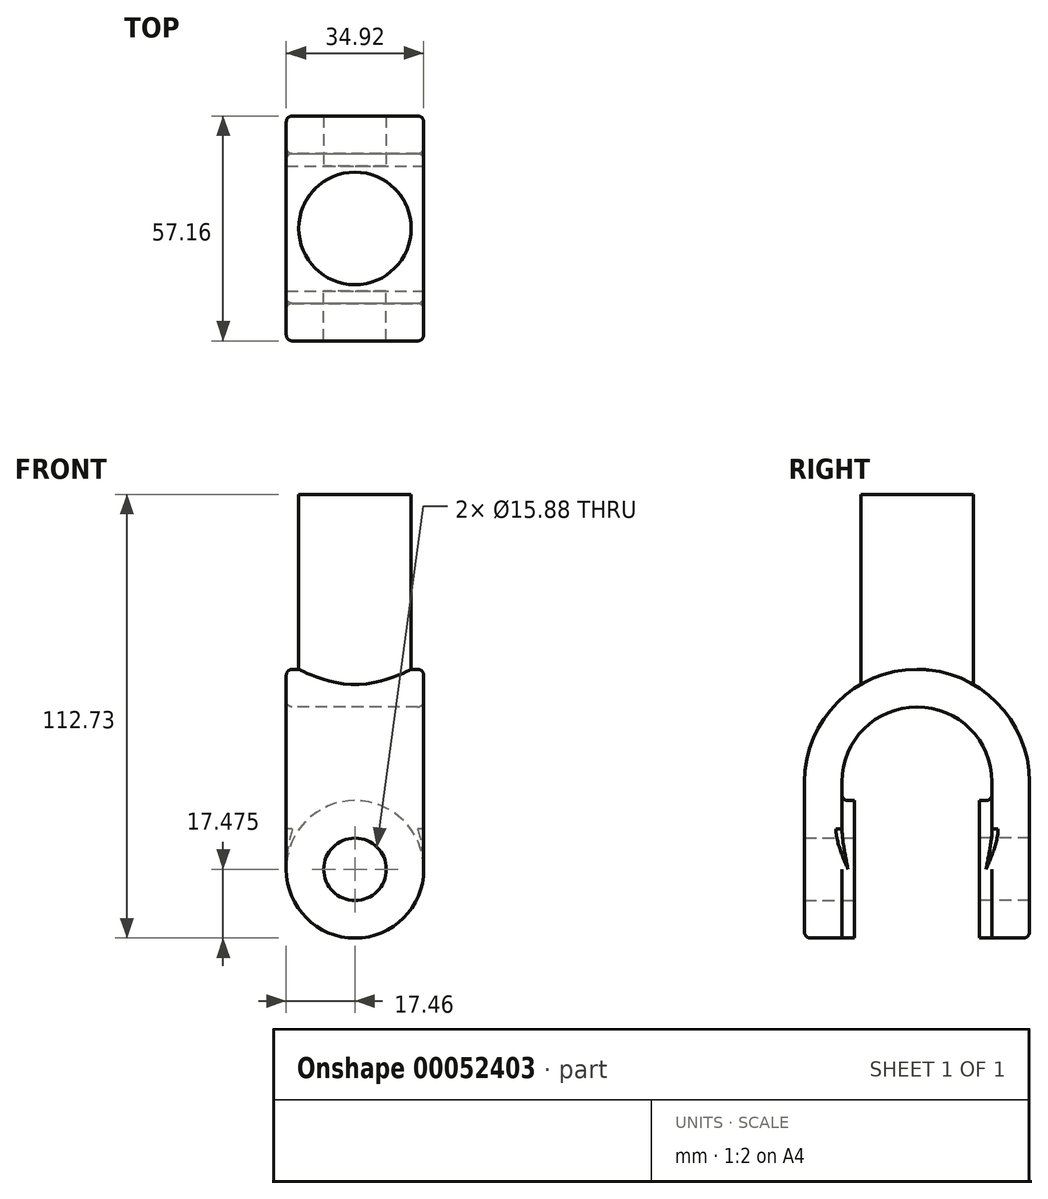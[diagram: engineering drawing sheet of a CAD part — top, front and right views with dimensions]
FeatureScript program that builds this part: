
annotation { "Feature Type Name" : "Feature", "Feature Type Description" : "" }
export const myFeature = defineFeature(function(context is Context, id is Id, definition is map)
    precondition{}
    {
        {
            var Q0;
            Q0=qCreatedBy(makeId("Right.planeOp"),FACE);
            var sketch = newSketch(context, id + "F0", { "sketchPlane" : qUnion([Q0])});
            skArc(sketch, "E0", {"start": v(19.05, 0) * mm, "mid": v(0, 19.05) * mm, "end": v(-19.05, 0) * mm});
            skArc(sketch, "E1.0", {"start": v(28.58, 0) * mm, "mid": v(0, 28.58) * mm, "end": v(-28.58, 0) * mm});
            skLineSegment(sketch, "E2", {"start": v(-28.58, 0) * mm, "end": v(-28.57, -39.7) * mm});
            skLineSegment(sketch, "E3", {"start": v(-28.57, -39.7) * mm, "end": v(-19.05, -39.7) * mm});
            skLineSegment(sketch, "E4", {"start": v(28.57, 0) * mm, "end": v(28.57, -39.7) * mm});
            skLineSegment(sketch, "E5", {"start": v(-19.05, 0) * mm, "end": v(-19.05, -39.7) * mm});
            skLineSegment(sketch, "E6", {"start": v(19.05, 0) * mm, "end": v(19.05, -39.7) * mm});
            skLineSegment(sketch, "E7.trimOffspring", {"start": v(19.05, -39.7) * mm, "end": v(28.57, -39.7) * mm});
            skSolve(sketch);
        }
        {
            var Q0;
            Q0=makeQuery(id+"F0.imprint","IMPRINT",FACE,{"disambiguationData":[TD([[makeQuery(id+"F0.imprint","IMPRINT",EDGE,{"derivedFrom":sQuery(id+"F0.wireOp",EDGE,"E0")}),-1.0]])]});
            extrude(context, id + "F1", {"entities" : qUnion([Q0]), "endBound" : BoundingType.SYMMETRIC, "depth" : 34.92 * mm});
        }
        {
            var Q0;
            Q0=qCreatedBy(makeId("Top.planeOp"),FACE);
            cPlane(context, id + "F2", {"entities" : qUnion([Q0]), "cplaneType" : CPlaneType.OFFSET, "offset" : 73.02 * mm, "width" : 152.4 * mm, "height" : 152.4 * mm});
        }
        {
            var Q0;
            Q0=qCreatedBy(id+"F2.planeOp",FACE);
            var sketch = newSketch(context, id + "F3", { "sketchPlane" : qUnion([Q0])});
            skCircle(sketch, "E8", {"center": v(0, 0) * mm, "radius": 14.29 * mm});
            skSolve(sketch);
        }
        {
            var Q0;
            Q0=makeQuery(id+"F3.imprint","IMPRINT",FACE,{"disambiguationData":[TD([[makeQuery(id+"F3.imprint","IMPRINT",EDGE,{"derivedFrom":sQuery(id+"F3.wireOp",EDGE,"E8")}),1.0]])]});
            extrude(context, id + "F4", {"entities" : qUnion([Q0]), "endBound" : BoundingType.UP_TO_NEXT, "oppositeDirection" : true, "depth" : 25.4 * mm});
        }
        {
            var Q0;
            Q0=makeQuery(id+"F1.opExtrude","CAP_EDGE",EDGE,{"disambiguationData":[OSD([sQuery(id+"F0.wireOp",EDGE,"E7.trimOffspring")])],"isStart":true});
            var Q1;
            Q1=makeQuery(id+"F1.opExtrude","CAP_EDGE",EDGE,{"disambiguationData":[OSD([sQuery(id+"F0.wireOp",EDGE,"E7.trimOffspring")])],"isStart":false});
            var Q2;
            Q2=makeQuery(id+"F1.opExtrude","CAP_EDGE",EDGE,{"disambiguationData":[OSD([sQuery(id+"F0.wireOp",EDGE,"E3")])],"isStart":true});
            var Q3;
            Q3=makeQuery(id+"F1.opExtrude","CAP_EDGE",EDGE,{"disambiguationData":[OSD([sQuery(id+"F0.wireOp",EDGE,"E3")])],"isStart":false});
            fillet(context, id + "F5", {"entities" : qUnion([Q0, Q1, Q2, Q3]), "radius" : 17.46 * mm, "tangentPropagation" : true, "allowEdgeOverflow" : false});
        }
        {
            var Q0;
            Q0=makeQuery(id+"F1.opExtrude","SWEPT_FACE",FACE,{"disambiguationData":[OSD([sQuery(id+"F0.wireOp",EDGE,"E6")])]});
            var sketch = newSketch(context, id + "F6", { "sketchPlane" : qUnion([Q0])});
            skCircle(sketch, "E9", {"center": v(0, -22.22) * mm, "radius": 17.46 * mm});
            skSolve(sketch);
        }
        {
            var Q0;
            Q0 = qSketchRegion(id + "F6", true);
            extrude(context, id + "F7", {"entities" : qUnion([Q0]), "operationType" : NewBodyOperationType.ADD, "depth" : 3.17 * mm});
        }
        {
            var Q0;
            Q0=makeQuery(id+"F1.opExtrude","SWEPT_BODY",BODY,{"disambiguationData":[OSD([sQuery(id+"F0.wireOp",EDGE,"E0"),sQuery(id+"F0.wireOp",EDGE,"E1.0"),sQuery(id+"F0.wireOp",EDGE,"E2"),sQuery(id+"F0.wireOp",EDGE,"E3"),sQuery(id+"F0.wireOp",EDGE,"E4"),sQuery(id+"F0.wireOp",EDGE,"E5"),sQuery(id+"F0.wireOp",EDGE,"E6"),sQuery(id+"F0.wireOp",EDGE,"E7.trimOffspring")])]});
            var Q1;
            Q1=qCreatedBy(makeId("Front.planeOp"),FACE);
            mirror(context, id + "F8", {"operationType" : NewBodyOperationType.ADD, "entities" : qUnion([Q0]), "mirrorPlane" : qUnion([Q1])});
        }
        {
            var Q0;
            Q0=makeQuery(id+"F7.opExtrude","CAP_FACE",FACE,{"disambiguationData":[OSD([sQuery(id+"F6.wireOp",EDGE,"E9")])],"isStart":false});
            var sketch = newSketch(context, id + "F9", { "sketchPlane" : qUnion([Q0])});
            skCircle(sketch, "E10", {"center": v(0, -22.22) * mm, "radius": 7.94 * mm});
            skSolve(sketch);
        }
        {
            var Q0;
            Q0 = qSketchRegion(id + "F9", true);
            extrude(context, id + "F10", {"entities" : qUnion([Q0]), "operationType" : NewBodyOperationType.REMOVE, "endBound" : BoundingType.THROUGH_ALL, "oppositeDirection" : true, "depth" : 25.4 * mm});
        }
        {
            var Q0;
            Q0=makeQuery(id+"F8.opPattern","COPY",FACE,{"derivedFrom":makeQuery(id+"F7.opExtrude","CAP_FACE",FACE,{"disambiguationData":[OSD([sQuery(id+"F6.wireOp",EDGE,"E9")])],"isStart":false}),"instanceName":"1"});
            var sketch = newSketch(context, id + "F11", { "sketchPlane" : qUnion([Q0])});
            skCircle(sketch, "E11", {"center": v(0, -22.22) * mm, "radius": 7.94 * mm});
            skSolve(sketch);
        }
        {
            var Q0;
            Q0 = qSketchRegion(id + "F11", true);
            extrude(context, id + "F12", {"entities" : qUnion([Q0]), "operationType" : NewBodyOperationType.REMOVE, "oppositeDirection" : true, "depth" : 25.4 * mm});
        }
        {
            var Q0;
            Q0=makeQuery(id+"F4.opExtrude","TWEAK_EDGE",EDGE,{"derivedFrom":[makeQuery(id+"F1.opExtrude","SWEPT_FACE",FACE,{"disambiguationData":[OSD([sQuery(id+"F0.wireOp",EDGE,"E1.0")])]}),makeQuery(id+"F3.imprint","IMPRINT",EDGE,{"derivedFrom":sQuery(id+"F3.wireOp",EDGE,"E8")})]});
            var Q1;
            {var subQ0=sQuery(id+"F0.wireOp",EDGE,"E7.trimOffspring");var subQ1=sQuery(id+"F0.wireOp",EDGE,"E6");var subQ2=sQuery(id+"F0.wireOp",EDGE,"E5");var subQ3=sQuery(id+"F0.wireOp",EDGE,"E4");var subQ4=sQuery(id+"F0.wireOp",EDGE,"E3");var subQ5=sQuery(id+"F0.wireOp",EDGE,"E2");var subQ6=sQuery(id+"F0.wireOp",EDGE,"E1.0");var subQ7=sQuery(id+"F0.wireOp",EDGE,"E0");var subQ8=sQuery(id+"F6.wireOp",EDGE,"E9");Q1=makeQuery(id+"F7.boolean.opBoolean","SPLIT",EDGE,{"disambiguationData":[TD([makeQuery(id+"F1.opExtrude","CAP_FACE",FACE,{"disambiguationData":[OSD([subQ7,subQ6,subQ5,subQ4,subQ3,subQ2,subQ1,subQ0])],"isStart":true}),makeQuery(id+"F1.opExtrude","CAP_FACE",FACE,{"disambiguationData":[OSD([subQ7,subQ6,subQ5,subQ4,subQ3,subQ2,subQ1,subQ0])],"isStart":false}),makeQuery(id+"F1.opExtrude","SWEPT_FACE",FACE,{"disambiguationData":[OSD([subQ1])]}),makeQuery(id+"F7.opExtrude","SWEPT_FACE",FACE,{"disambiguationData":[OSD([subQ8])]})])],"derivedFrom":makeQuery(id+"F7.opExtrude","CAP_EDGE",EDGE,{"disambiguationData":[OSD([subQ8])],"isStart":true})});}
            var Q2;
            {var subQ0=sQuery(id+"F0.wireOp",EDGE,"E7.trimOffspring");var subQ1=sQuery(id+"F0.wireOp",EDGE,"E6");var subQ2=sQuery(id+"F0.wireOp",EDGE,"E5");var subQ3=sQuery(id+"F0.wireOp",EDGE,"E4");var subQ4=sQuery(id+"F0.wireOp",EDGE,"E3");var subQ5=sQuery(id+"F0.wireOp",EDGE,"E2");var subQ6=sQuery(id+"F0.wireOp",EDGE,"E1.0");var subQ7=sQuery(id+"F0.wireOp",EDGE,"E0");var subQ8=sQuery(id+"F6.wireOp",EDGE,"E9");Q2=makeQuery(id+"F8.opPattern","COPY",EDGE,{"derivedFrom":makeQuery(id+"F7.boolean.opBoolean","SPLIT",EDGE,{"disambiguationData":[TD([makeQuery(id+"F1.opExtrude","CAP_FACE",FACE,{"disambiguationData":[OSD([subQ7,subQ6,subQ5,subQ4,subQ3,subQ2,subQ1,subQ0])],"isStart":true}),makeQuery(id+"F1.opExtrude","CAP_FACE",FACE,{"disambiguationData":[OSD([subQ7,subQ6,subQ5,subQ4,subQ3,subQ2,subQ1,subQ0])],"isStart":false}),makeQuery(id+"F1.opExtrude","SWEPT_FACE",FACE,{"disambiguationData":[OSD([subQ1])]}),makeQuery(id+"F7.opExtrude","SWEPT_FACE",FACE,{"disambiguationData":[OSD([subQ8])]})])],"derivedFrom":makeQuery(id+"F7.opExtrude","CAP_EDGE",EDGE,{"disambiguationData":[OSD([subQ8])],"isStart":true})}),"instanceName":"1"});}
            fillet(context, id + "F13", {"entities" : qUnion([Q0, Q1, Q2]), "radius" : 1.52 * mm, "tangentPropagation" : true, "allowEdgeOverflow" : false});
        }
        {
            var Q0;
            Q0=makeQuery(id+"F5.opFillet","BLEND_EDGE",EDGE,{"blendedFrom":[makeQuery(id+"F1.opExtrude","CAP_EDGE",EDGE,{"disambiguationData":[OSD([sQuery(id+"F0.wireOp",EDGE,"E7.trimOffspring")])],"isStart":true}),makeQuery(id+"F1.opExtrude","SWEPT_FACE",FACE,{"disambiguationData":[OSD([sQuery(id+"F0.wireOp",EDGE,"E4")])]})],"blendedInto":[makeQuery(id+"F1.opExtrude","SWEPT_FACE",FACE,{"disambiguationData":[OSD([sQuery(id+"F0.wireOp",EDGE,"E4")])]})]});
            var Q1;
            Q1=makeQuery(id+"F5.opFillet","BLEND_EDGE",EDGE,{"blendedFrom":[makeQuery(id+"F1.opExtrude","CAP_EDGE",EDGE,{"disambiguationData":[OSD([sQuery(id+"F0.wireOp",EDGE,"E3")])],"isStart":true}),makeQuery(id+"F1.opExtrude","SWEPT_FACE",FACE,{"disambiguationData":[OSD([sQuery(id+"F0.wireOp",EDGE,"E2")])]})],"blendedInto":[makeQuery(id+"F1.opExtrude","SWEPT_FACE",FACE,{"disambiguationData":[OSD([sQuery(id+"F0.wireOp",EDGE,"E2")])]})]});
            fillet(context, id + "F14", {"entities" : qUnion([Q0, Q1]), "radius" : 1.52 * mm, "tangentPropagation" : true, "allowEdgeOverflow" : false});
        }
        {
            var Q0;
            Q0=makeQuery(id+"F1.opExtrude","CAP_EDGE",EDGE,{"disambiguationData":[OSD([sQuery(id+"F0.wireOp",EDGE,"E0")])],"isStart":false});
            var Q1;
            Q1=makeQuery(id+"F1.opExtrude","CAP_EDGE",EDGE,{"disambiguationData":[OSD([sQuery(id+"F0.wireOp",EDGE,"E0")])],"isStart":true});
            fillet(context, id + "F15", {"entities" : qUnion([Q0, Q1]), "radius" : 1.52 * mm, "tangentPropagation" : true, "allowEdgeOverflow" : false});
        }
    });
